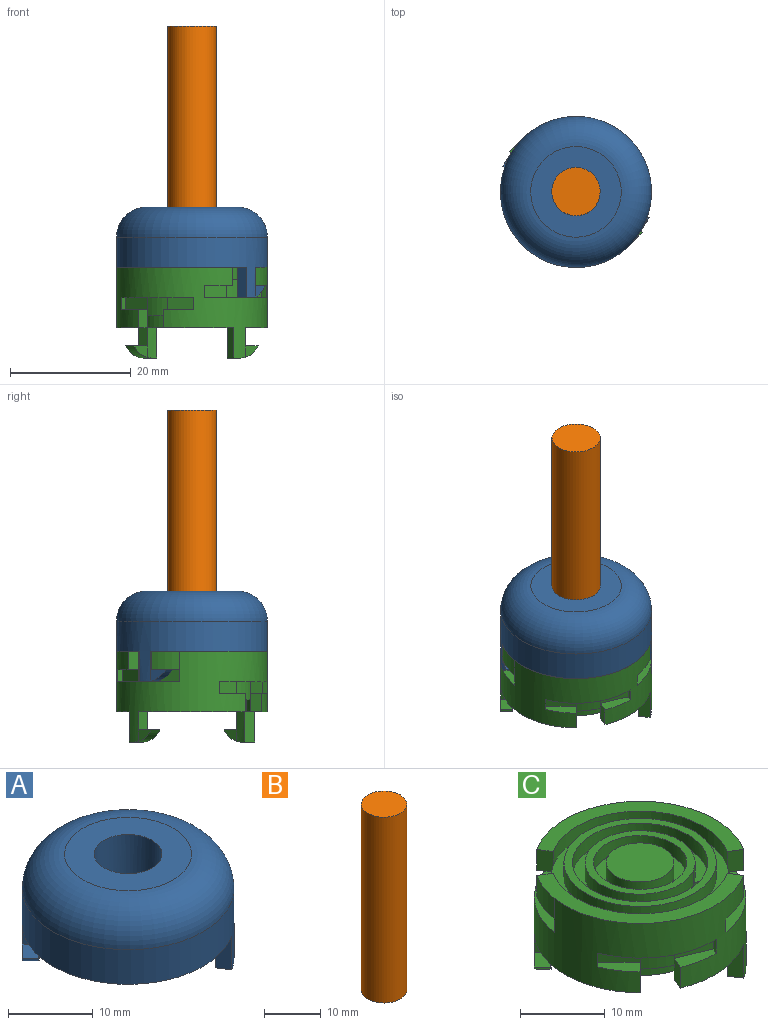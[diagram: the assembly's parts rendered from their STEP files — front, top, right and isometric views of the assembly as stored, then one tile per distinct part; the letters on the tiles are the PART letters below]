
ASSEMBLY  parts=3 mates=2
PART A: 52 faces, bbox 27.1x27.1x15 mm
  f0: cylinder r=4mm len=10mm, axis (0,0,-1), area 237.5mm2, adj f1,f2,f3,f17,f22,f41,f42,f43
  f1: plane 6.37x3.4mm, normal (0,0,-1), area 2mm2, adj f0,f10,f42,f49
  f2: plane 4.43x0.8mm, normal (0,0,-1), area 1.1mm2, adj f0,f11,f43,f50
  f3: plane 11x8.62mm, normal (0,0,-1), area 26.6mm2, adj f0,f8,f10,f18,f41,f42,f44,f49
  f4: plane 6.23x1.87mm, normal (0,0,-1), area 7.1mm2, adj f9,f11,f43,f50
  f5: cylinder r=6.5mm len=13mm, axis (0,0,-1), area 28.6mm2, adj f7,f16,f44,f49
  f6: cylinder r=6.5mm len=7.67mm, axis (0,0,-1), area 8.2mm2, adj f7,f25,f43,f50
  f7: plane 16x16mm, normal (0,0,-1), area 62.4mm2, adj f5,f6,f15,f43,f44,f46,f47,f49
  f8: cylinder r=5.5mm len=11mm, axis (0,0,-1), area 23.9mm2, adj f3,f16,f44,f49
  f9: cylinder r=5.5mm len=6.23mm, axis (0,0,-1), area 6.6mm2, adj f4,f25,f43,f50
  f10: cylinder r=4.25mm len=6.37mm, axis (0,0,1), area 8.1mm2, adj f1,f3,f42,f49
  f11: cylinder r=4.25mm len=4.43mm, axis (0,0,1), area 4.7mm2, adj f2,f4,f43,f50
  f12: cylinder r=9mm len=18mm, axis (0,0,-1), area 54.5mm2, adj f13,f24,f49,f50
  f13: plane 21x21mm, normal (0,0,-1), area 88.9mm2, adj f12,f21,f49,f50
  f14: plane 1.41x1.41mm, normal (0,0,-1), area 0.1mm2, adj f21,f48
  f15: cylinder r=8mm len=16mm, axis (0,0,-1), area 48.3mm2, adj f7,f24,f49,f50
  f16: plane 13x10.33mm, normal (0,0,-1), area 26.3mm2, adj f5,f8,f44,f49
  f17: plane 6.37x3.4mm, normal (0,0,-1), area 2mm2, adj f0,f18,f41,f44
  f18: cylinder r=4.25mm len=6.37mm, axis (0,0,1), area 8.1mm2, adj f3,f17,f41,f44
  f19: cylinder r=12.5mm len=25mm, axis (0,0,-1), area 417.2mm2, adj f20,f23,f26,f27,f28,f29,f30,f31
  f20: plane 21.34x19.44mm, normal (0,0,-1), area 67.7mm2, adj f19,f21,f27,f29
  f21: cylinder r=10.5mm len=21mm, axis (0,0,-1), area 86.6mm2, adj f13,f14,f20,f23,f26,f27,f28,f29
  f22: plane 15x15mm, normal (0,0,1), area 126.4mm2, adj f0,f40
  f23: plane 21.34x19.44mm, normal (0,0,-1), area 67.7mm2, adj f19,f21,f26,f30
  f24: plane 18x18mm, normal (0,0,-1), area 51.4mm2, adj f12,f15,f49,f50
  f25: plane 7.67x1.97mm, normal (0,0,-1), area 7.4mm2, adj f6,f9,f43,f50
  f26: plane 5x1.66mm, normal (0.83,0.56,0), area 10mm2, adj f19,f21,f23,f28
  f27: plane 3x1.43mm, normal (-0.71,-0.7,0), area 6mm2, adj f19,f20,f21,f32
  f28: plane 2.31x2.27mm, normal (0,0,-1), area 2.5mm2, adj f19,f21,f26,f39
  f29: plane 5x1.66mm, normal (-0.83,-0.56,0), area 10mm2, adj f19,f20,f21,f31
  f30: plane 3x1.41mm, normal (0.71,0.71,0), area 6mm2, adj f19,f21,f23,f35
  f31: plane 2.3x2.27mm, normal (0,0,-1), area 2.5mm2, adj f19,f21,f29,f38
  f32: plane 3.54x3.53mm, normal (0,0,1), area 6mm2, adj f27,f33,f34,f39
  f33: plane 2.14x2.1mm, normal (-0.7,0.71,0), area 3.6mm2, adj f19,f32,f39
  f34: plane 2.14x2.1mm, normal (0.7,-0.71,0), area 3.6mm2, adj f21,f32,f39
  f35: plane 3.54x3.54mm, normal (0,0,1), area 6mm2, adj f30,f36,f37,f38
  f36: plane 2.12x2.12mm, normal (0.71,-0.71,0), area 3.6mm2, adj f19,f35,f38
  f37: plane 2.12x2.12mm, normal (-0.71,0.71,0), area 3.6mm2, adj f21,f35,f38
  f38: cylinder r=5mm len=4.28mm, axis (0.71,-0.71,0), area 9.3mm2, adj f19,f21,f31,f35,f36,f37
  f39: cylinder r=5mm len=4.28mm, axis (-0.7,0.71,0), area 9.3mm2, adj f19,f21,f28,f32,f33,f34
  f40: torus R=7.5mm, axis (0,0,1), area 527.2mm2, adj f19,f22
  f41: plane 1x0.24mm, normal (0.98,-0.21,0), area 0.3mm2, adj f0,f3,f17,f18
  f42: plane 1x0.24mm, normal (-0.98,-0.21,0), area 0.3mm2, adj f0,f1,f3,f10
  f43: plane 3x2.58mm, normal (-0.71,-0.71,0), area 8.6mm2, adj f0,f2,f4,f6,f7,f9,f11,f25
  f44: plane 3x2.87mm, normal (0.71,0.71,0), area 9.4mm2, adj f0,f3,f5,f7,f8,f16,f17,f18
  f45: plane 4.28x4.28mm, normal (0,0,-1), area 7.9mm2, adj f0,f43,f44,f46,f47
  f46: plane 2x1.41mm, normal (0.71,-0.71,0), area 4mm2, adj f7,f44,f45,f47
  f47: plane 2x0.29mm, normal (-0.7,-0.71,0), area 0.8mm2, adj f7,f43,f45,f46
  f48: plane 2x1.41mm, normal (-0.71,-0.71,0), area 4mm2, adj f14,f49,f50,f51
  f49: plane 4.65x4.65mm, normal (-0.71,0.71,0), area 15.4mm2, adj f0,f1,f3,f5,f7,f8,f10,f12
  f50: plane 4.65x4.65mm, normal (0.71,-0.71,0), area 15.4mm2, adj f0,f2,f4,f6,f7,f9,f11,f12
  f51: plane 6.07x6.07mm, normal (0,0,-1), area 13mm2, adj f0,f48,f49,f50
PART B: 3 faces, bbox 8x8x40 mm
  f0: cylinder r=4mm len=40mm, axis (0,0,-1), area 1005.3mm2, adj f1,f2
  f1: plane 8x8mm, normal (0,0,1), area 50.3mm2, adj f0
  f2: plane 8x8mm, normal (0,0,-1), area 50.3mm2, adj f0
PART C: 91 faces, bbox 25x25x15 mm
  f0: plane 2x0.88mm, normal (-0.92,0.38,0), area 1.9mm2, adj f1,f9,f36,f90
  f1: plane 4.62x2mm, normal (-0.38,-0.92,0), area 10mm2, adj f0,f34,f36,f90
  f2: plane 3.54x3.54mm, normal (-0.71,-0.71,0), area 10mm2, adj f34,f36,f51,f89
  f3: plane 3.54x3.54mm, normal (0.71,0.71,0), area 10mm2, adj f37,f38,f52,f88
  f4: plane 2x0.88mm, normal (0.92,-0.38,0), area 1.9mm2, adj f5,f9,f38,f87
  f5: plane 4.62x2mm, normal (0.38,0.92,0), area 10mm2, adj f4,f37,f38,f87
  f6: plane 11x11mm, normal (0,0,1), area 43mm2, adj f30,f81,f83
  f7: plane 19.26x19.26mm, normal (0,0,1), area 62.4mm2, adj f9,f10,f11,f58,f72
  f8: plane 3x1.68mm, normal (-0.84,-0.54,0), area 6mm2, adj f9,f13,f57,f70,f73
  f9: cylinder r=12.5mm len=25mm, axis (0,0,-1), area 609.6mm2, adj f0,f4,f7,f8,f10,f11,f12,f13
  f10: cylinder r=12.5mm len=4.77mm, axis (0,0,-1), area 15.4mm2, adj f7,f9,f58,f67
  f11: plane 3x1.68mm, normal (0.84,0.54,0), area 6mm2, adj f7,f9,f55,f64,f72
  f12: plane 3x1.68mm, normal (-0.54,-0.84,0), area 6mm2, adj f9,f13,f55,f61,f73
  f13: plane 19.26x19.26mm, normal (0,0,1), area 62.4mm2, adj f8,f9,f12,f73
  f14: plane 3x1.41mm, normal (-0.71,0.71,0), area 6mm2, adj f9,f17,f20,f37,f88
  f15: plane 3x1.85mm, normal (-0.92,0.38,0), area 6mm2, adj f9,f19,f20,f34,f90
  f16: plane 3x1.85mm, normal (0.92,-0.38,0), area 6mm2, adj f9,f21,f22,f37,f87
  f17: plane 17.68x5.08mm, normal (0,0,-1), area 36.1mm2, adj f9,f14,f20,f43
  f18: plane 17.68x5.08mm, normal (0,0,-1), area 36.1mm2, adj f9,f21,f35,f40
  f19: plane 11.73x3.77mm, normal (0,0,-1), area 22.6mm2, adj f9,f15,f20,f42
  f20: cylinder r=10.5mm len=17.92mm, axis (0,0,-1), area 68mm2, adj f14,f15,f17,f19,f24,f42,f43,f44
  f21: cylinder r=10.5mm len=17.92mm, axis (0,0,-1), area 68.1mm2, adj f16,f18,f22,f24,f35,f39,f40,f41
  f22: plane 11.73x3.77mm, normal (0,0,-1), area 22.6mm2, adj f9,f16,f21,f39
  f23: cylinder r=9mm len=18mm, axis (0,0,-1), area 113.1mm2, adj f24,f25
  f24: plane 21x21mm, normal (0,0,-1), area 90.1mm2, adj f20,f21,f23,f34,f37,f86
  f25: plane 18x18mm, normal (0,0,-1), area 53.4mm2, adj f23,f27
  f26: cylinder r=6.5mm len=13mm, axis (0,0,-1), area 81.7mm2, adj f28,f29,f85
  f27: cylinder r=8mm len=16mm, axis (0,0,-1), area 100.5mm2, adj f25,f28
  f28: plane 16x16mm, normal (0,0,-1), area 66.6mm2, adj f26,f27,f84
  f29: plane 13x13mm, normal (0,0,-1), area 37.7mm2, adj f26,f31
  f30: cylinder r=4mm len=10mm, axis (0,0,-1), area 100.7mm2, adj f6,f32,f33,f82,f83
  f31: cylinder r=5.5mm len=11mm, axis (0,0,-1), area 69.1mm2, adj f29,f32
  f32: plane 11x11mm, normal (0,0,-1), area 43mm2, adj f30,f31,f83
  f33: plane 8x8mm, normal (0,0,-1), area 50.3mm2, adj f30
  f34: cylinder r=10.5mm len=3.41mm, axis (0,0,-1), area 12.4mm2, adj f1,f2,f15,f24,f35,f36
  f35: plane 3x1.41mm, normal (0.71,-0.71,0), area 6mm2, adj f9,f18,f21,f34,f89
  f36: plane 12.24x8.61mm, normal (0,0,-1), area 25.6mm2, adj f0,f1,f2,f9,f34,f51
  f37: cylinder r=10.5mm len=3.41mm, axis (0,0,-1), area 12.4mm2, adj f3,f5,f14,f16,f24,f38
  f38: plane 12.24x8.61mm, normal (0,0,-1), area 25.6mm2, adj f3,f4,f5,f9,f37,f52
  f39: plane 5x1.66mm, normal (0.83,0.56,0), area 10mm2, adj f9,f21,f22,f41
  f40: plane 3x1.43mm, normal (-0.71,-0.7,0), area 6mm2, adj f9,f18,f21,f45
  f41: plane 2.31x2.27mm, normal (0,0,-1), area 2.5mm2, adj f9,f21,f39,f54
  f42: plane 5x1.66mm, normal (-0.83,-0.56,0), area 10mm2, adj f9,f19,f20,f44
  f43: plane 3x1.41mm, normal (0.71,0.71,0), area 6mm2, adj f9,f17,f20,f48
  f44: plane 2.3x2.27mm, normal (0,0,-1), area 2.5mm2, adj f9,f20,f42,f53
  f45: plane 3.54x3.53mm, normal (0,0,1), area 6mm2, adj f40,f46,f47,f54
  f46: plane 2.14x2.1mm, normal (-0.7,0.71,0), area 3.6mm2, adj f9,f45,f54
  f47: plane 2.14x2.1mm, normal (0.7,-0.71,0), area 3.6mm2, adj f21,f45,f54
  f48: plane 3.54x3.54mm, normal (0,0,1), area 6mm2, adj f43,f49,f50,f53
  f49: plane 2.12x2.12mm, normal (0.71,-0.71,0), area 3.6mm2, adj f9,f48,f53
  f50: plane 2.12x2.12mm, normal (-0.71,0.71,0), area 3.6mm2, adj f20,f48,f53
  f51: plane 2x0.68mm, normal (0.71,-0.71,0), area 1.9mm2, adj f2,f9,f36,f89
  f52: plane 2x0.68mm, normal (-0.71,0.71,0), area 1.9mm2, adj f3,f9,f38,f88
  f53: cylinder r=5mm len=4.28mm, axis (0.71,-0.71,0), area 9.3mm2, adj f9,f20,f44,f48,f49,f50
  f54: cylinder r=5mm len=4.28mm, axis (-0.7,0.71,0), area 9.3mm2, adj f9,f21,f41,f45,f46,f47
  f55: cylinder r=10.5mm len=3.15mm, axis (0,0,1), area 13.5mm2, adj f11,f12,f56,f62,f65,f75
  f56: plane 10.87x10.87mm, normal (0,0,1), area 26.4mm2, adj f9,f55,f60,f62,f63,f65
  f57: cylinder r=10.5mm len=3.15mm, axis (0,0,1), area 13.5mm2, adj f8,f58,f59,f68,f71,f75
  f58: plane 3x1.68mm, normal (0.54,0.84,0), area 6mm2, adj f7,f10,f57,f67,f72
  f59: plane 10.87x10.87mm, normal (0,0,1), area 26.4mm2, adj f9,f57,f66,f68,f69,f71
  f60: plane 2x0.8mm, normal (-0.54,-0.84,0), area 1.9mm2, adj f9,f56,f61,f62
  f61: plane 5.29x3.51mm, normal (0,0,-1), area 8.3mm2, adj f9,f12,f60,f62
  f62: plane 4.21x2.71mm, normal (0.84,-0.54,0), area 10mm2, adj f55,f56,f60,f61
  f63: plane 2x0.8mm, normal (0.84,0.54,0), area 1.9mm2, adj f9,f56,f64,f65
  f64: plane 5.29x3.51mm, normal (0,0,-1), area 8.3mm2, adj f9,f11,f63,f65
  f65: plane 4.21x2.71mm, normal (0.54,-0.84,0), area 10mm2, adj f55,f56,f63,f64
  f66: plane 2x0.8mm, normal (0.54,0.84,0), area 1.9mm2, adj f9,f59,f67,f68
  f67: plane 5.29x3.51mm, normal (0,0,-1), area 8.3mm2, adj f10,f58,f66,f68
  f68: plane 4.21x2.71mm, normal (-0.84,0.54,0), area 10mm2, adj f57,f59,f66,f67
  f69: plane 2x0.8mm, normal (-0.84,-0.54,0), area 1.9mm2, adj f9,f59,f70,f71
  f70: plane 5.29x3.51mm, normal (0,0,-1), area 8.3mm2, adj f8,f9,f69,f71
  f71: plane 4.21x2.71mm, normal (-0.54,0.84,0), area 10mm2, adj f57,f59,f69,f70
  f72: cylinder r=10.5mm len=16.18mm, axis (0,0,1), area 57mm2, adj f7,f11,f58,f75
  f73: cylinder r=10.5mm len=16.18mm, axis (0,0,1), area 57mm2, adj f8,f12,f13,f75
  f74: cylinder r=9mm len=18mm, axis (0,0,1), area 113.1mm2, adj f75,f76
  f75: plane 21x21mm, normal (0,0,1), area 90.1mm2, adj f55,f57,f72,f73,f74,f86
  f76: plane 18x18mm, normal (0,0,1), area 53.4mm2, adj f74,f78
  f77: cylinder r=6.5mm len=13mm, axis (0,0,1), area 81.3mm2, adj f79,f80,f84
  f78: cylinder r=8mm len=16mm, axis (0,0,1), area 100.5mm2, adj f76,f79
  f79: plane 16x16mm, normal (0,0,1), area 66.6mm2, adj f77,f78,f84
  f80: plane 13x13mm, normal (0,0,1), area 37.7mm2, adj f77,f81,f84
  f81: cylinder r=5.5mm len=11mm, axis (0,0,1), area 69.1mm2, adj f6,f80
  f82: plane 8x8mm, normal (0,0,1), area 50.3mm2, adj f30
  f83: cylinder r=0.75mm len=6mm, axis (0,0,-1), area 28.1mm2, adj f6,f30,f32
  f84: cylinder r=0.75mm len=8mm, axis (0,0,-1), area 28.7mm2, adj f28,f77,f79,f80,f85
  f85: plane 0.18x0.1mm, normal (0,0,1), area 0mm2, adj f26,f84
  f86: cylinder r=0.75mm len=6mm, axis (0,0,-1), area 28.2mm2, adj f24,f75
  f87: plane 5.38x2.8mm, normal (0,0,1), area 8.3mm2, adj f4,f5,f9,f16
  f88: plane 4.95x4.21mm, normal (0,0,1), area 8.3mm2, adj f3,f9,f14,f52
  f89: plane 4.95x4.21mm, normal (0,0,1), area 8.3mm2, adj f2,f9,f35,f51
  f90: plane 5.38x2.8mm, normal (0,0,1), area 8.3mm2, adj f0,f1,f9,f15
PLACE A rot(axis=(0,0,1),12deg) t=(-3.4,-1.47,8.3)mm
PLACE B rot(axis=(0,0,1),12deg) t=(-3.4,-1.47,8.3)mm
PLACE C t=(-3.4,-1.47,-1.7)mm fixed
MATE fastened B.f0 <-> A.f0  axis (0,0,-1) through (-3.4,-1.47,8.3)mm
MATE cylindrical A.f0 <-> C.f9  axis (0,0,-1) through (-3.4,-1.47,8.3)mm
